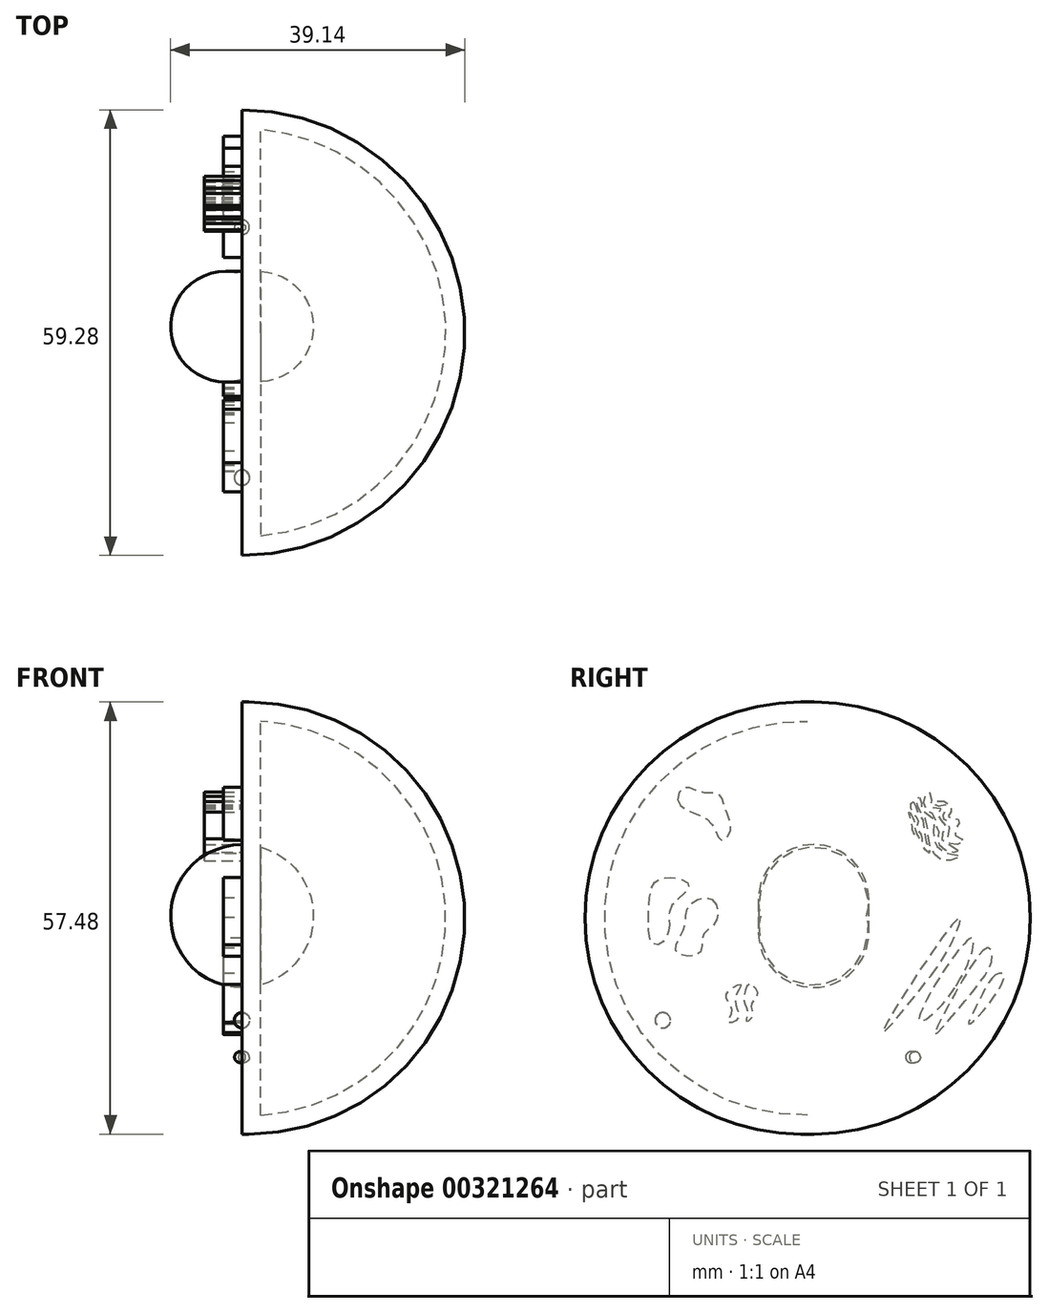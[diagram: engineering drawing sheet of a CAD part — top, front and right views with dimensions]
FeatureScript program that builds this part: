
annotation { "Feature Type Name" : "Feature", "Feature Type Description" : "" }
export const myFeature = defineFeature(function(context is Context, id is Id, definition is map)
    precondition{}
    {
        {
            var Q0;
            Q0=qCreatedBy(makeId("Front.planeOp"),FACE);
            var sketch = newSketch(context, id + "F0", { "sketchPlane" : qUnion([Q0])});
            skLineSegment(sketch, "E0", {"start": v(0, 0) * mm, "end": v(0, 57.46) * mm});
            skArc(sketch, "E1", {"start": v(0, 0) * mm, "mid": v(29.64, 28.73) * mm, "end": v(0, 57.46) * mm});
            skSolve(sketch);
        }
        {
            var Q0;
            Q0 = qSketchRegion(id + "F0", true);
            var Q1;
            Q1=sQuery(id+"F0.wireOp",EDGE,"E0");
            revolve(context, id + "F1", {"entities" : qUnion([Q0]), "axis" : qUnion([Q1]), "revolveType" : RevolveType.SYMMETRIC, "angle" : 180 * degree});
        }
        {
            var Q0;
            Q0=makeQuery(id+"F1.opRevolve","CAP_FACE",FACE,{"disambiguationData":[OSD([sQuery(id+"F0.wireOp",EDGE,"E0"),sQuery(id+"F0.wireOp",EDGE,"E1")])],"isStart":false});
            var Q1;
            Q1=makeQuery(id+"F1.opRevolve","SWEPT_BODY",BODY,{"disambiguationData":[OSD([sQuery(id+"F0.wireOp",EDGE,"E0"),sQuery(id+"F0.wireOp",EDGE,"E1")])]});
            shell(context, id + "F2", {"isHollow" : true, "entities" : qUnion([Q0]), "parts" : qUnion([Q1]), "thickness" : 2.5 * mm});
        }
        {
            var Q0;
            Q0=qCreatedBy(makeId("Right.planeOp"),FACE);
            var sketch = newSketch(context, id + "F3", { "sketchPlane" : qUnion([Q0])});
            skLineSegment(sketch, "E2", {"start": v(7.83, 29) * mm, "end": v(-6.24, 29) * mm});
            skArc(sketch, "E3", {"start": v(7.83, 29) * mm, "mid": v(0.8, 38.5) * mm, "end": v(-6.24, 29) * mm});
            skSolve(sketch);
        }
        {
            var Q0;
            Q0 = qSketchRegion(id + "F3", true);
            var Q1;
            Q1=sQuery(id+"F3.wireOp",EDGE,"E2");
            revolve(context, id + "F4", {"operationType" : NewBodyOperationType.ADD, "entities" : qUnion([Q0]), "axis" : qUnion([Q1]), "revolveType" : RevolveType.ONE_DIRECTION, "angle" : 360 * degree});
        }
        {
            var Q0;
            Q0=makeQuery(id+"F1.opRevolve","CAP_FACE",FACE,{"disambiguationData":[OSD([sQuery(id+"F0.wireOp",EDGE,"E0"),sQuery(id+"F0.wireOp",EDGE,"E1")])],"isStart":false});
            var sketch = newSketch(context, id + "F5", { "sketchPlane" : qUnion([Q0])});
            skLineSegment(sketch, "E4", {"start": v(-14.03, 9.55) * mm, "end": v(-14.03, 10.91) * mm});
            skArc(sketch, "E5", {"start": v(-14.03, 10.91) * mm, "mid": v(-15, 10.23) * mm, "end": v(-14.03, 9.55) * mm});
            skSolve(sketch);
        }
        {
            var Q0;
            Q0 = qSketchRegion(id + "F5", true);
            var Q1;
            Q1=sQuery(id+"F5.wireOp",EDGE,"E4");
            revolve(context, id + "F6", {"entities" : qUnion([Q0]), "axis" : qUnion([Q1]), "revolveType" : RevolveType.FULL});
        }
        {
            var Q0;
            Q0=makeQuery(id+"F1.opRevolve","CAP_FACE",FACE,{"disambiguationData":[OSD([sQuery(id+"F0.wireOp",EDGE,"E0"),sQuery(id+"F0.wireOp",EDGE,"E1")])],"isStart":false});
            var sketch = newSketch(context, id + "F7", { "sketchPlane" : qUnion([Q0])});
            skEllipse(sketch, "E6", {"center": v(-17.37, 40.2) * mm, "majorRadius": 5.81 * mm, "minorRadius": 3.58 * mm, "majorAxis": v(0.42, 0.9)});
            skSolve(sketch);
        }
        {
            var Q0;
            Q0 = qSketchRegion(id + "F7", true);
            var Q1;
            Q1=sQuery(id+"F7.wireOp",EDGE,"E6");
            extrude(context, id + "F8", {"entities" : qUnion([Q0]), "bodyType" : ToolBodyType.SURFACE, "operationType" : NewBodyOperationType.ADD, "surfaceEntities" : qUnion([Q1]), "depth" : 5 * mm});
        }
        {
            var Q0;
            Q0=makeQuery(id+"F1.opRevolve","CAP_FACE",FACE,{"disambiguationData":[OSD([sQuery(id+"F0.wireOp",EDGE,"E0"),sQuery(id+"F0.wireOp",EDGE,"E1")])],"isStart":false});
            var sketch = newSketch(context, id + "F9", { "sketchPlane" : qUnion([Q0])});
            skFitSpline(sketch, "E7", {"points": [v(-17.23, 44.31) * mm, v(-19.19, 43.32) * mm, v(-18.73, 42.1) * mm, v(-20.22, 41.78) * mm, v(-19.53, 39.95) * mm, v(-20.82, 38.97) * mm, v(-18.9, 38.67) * mm, v(-18.84, 41.42) * mm, v(-18, 42.05) * mm, v(-18.5, 43.71) * mm, v(-17.06, 43.6) * mm, v(-17.23, 44.31) * mm]});
            skSolve(sketch);
        }
        {
            var Q0;
            Q0 = qSketchRegion(id + "F9", true);
            extrude(context, id + "F10", {"entities" : qUnion([Q0]), "depth" : 5 * mm});
        }
        {
            var Q0;
            Q0=makeQuery(id+"F1.opRevolve","CAP_FACE",FACE,{"disambiguationData":[OSD([sQuery(id+"F0.wireOp",EDGE,"E0"),sQuery(id+"F0.wireOp",EDGE,"E1")])],"isStart":false});
            var sketch = newSketch(context, id + "F11", { "sketchPlane" : qUnion([Q0])});
            skFitSpline(sketch, "E8", {"points": [v(-20.04, 37.68) * mm, v(-17.83, 39.3) * mm, v(-18.45, 41) * mm, v(-17.3, 42.39) * mm, v(-17.76, 43.35) * mm, v(-16.54, 43.34) * mm, v(-16.56, 44.83) * mm, v(-15.88, 45.44) * mm, v(-15.54, 43.4) * mm, v(-16.67, 42.57) * mm, v(-17.18, 40.8) * mm, v(-17.46, 40.28) * mm, v(-17.37, 38.77) * mm, v(-19.06, 37.55) * mm, v(-20.04, 37.68) * mm]});
            skSolve(sketch);
        }
        {
            var Q0;
            Q0 = qSketchRegion(id + "F11", true);
            extrude(context, id + "F12", {"entities" : qUnion([Q0]), "operationType" : NewBodyOperationType.ADD, "depth" : 5 * mm});
        }
        {
            var Q0;
            Q0=makeQuery(id+"F1.opRevolve","CAP_FACE",FACE,{"disambiguationData":[OSD([sQuery(id+"F0.wireOp",EDGE,"E0"),sQuery(id+"F0.wireOp",EDGE,"E1")])],"isStart":false});
            var sketch = newSketch(context, id + "F13", { "sketchPlane" : qUnion([Q0])});
            skFitSpline(sketch, "E9", {"points": [v(-19.9, 36.75) * mm, v(-17.85, 36.46) * mm, v(-16.17, 38.81) * mm, v(-15.73, 41.79) * mm, v(-14.8, 43.18) * mm, v(-14.63, 44.9) * mm, v(-15.07, 44.5) * mm, v(-15.2, 43.16) * mm, v(-16.5, 42.2) * mm, v(-16.77, 40.51) * mm, v(-17.04, 38.58) * mm, v(-18.78, 37.27) * mm, v(-19.97, 37.1) * mm, v(-19.9, 36.75) * mm]});
            skSolve(sketch);
        }
        {
            var Q0;
            Q0 = qSketchRegion(id + "F13", true);
            extrude(context, id + "F14", {"entities" : qUnion([Q0]), "depth" : 5 * mm});
        }
        {
            var Q0;
            Q0=makeQuery(id+"F1.opRevolve","CAP_FACE",FACE,{"disambiguationData":[OSD([sQuery(id+"F0.wireOp",EDGE,"E0"),sQuery(id+"F0.wireOp",EDGE,"E1")])],"isStart":false});
            var sketch = newSketch(context, id + "F15", { "sketchPlane" : qUnion([Q0])});
            skFitSpline(sketch, "E10", {"points": [v(-14.1, 44.2) * mm, v(-14.78, 42.45) * mm, v(-15.3, 41.89) * mm, v(-15.46, 40.73) * mm, v(-15.75, 38.96) * mm, v(-15.94, 38.38) * mm, v(-16.24, 37.35) * mm, v(-15.31, 38.38) * mm, v(-15.24, 39.62) * mm, v(-14.63, 40.63) * mm, v(-14.75, 41.76) * mm, v(-14.14, 42.53) * mm, v(-13.72, 43.86) * mm, v(-14.1, 44.2) * mm]});
            skSolve(sketch);
        }
        {
            var Q0;
            Q0 = qSketchRegion(id + "F15", true);
            extrude(context, id + "F16", {"entities" : qUnion([Q0]), "depth" : 5 * mm});
        }
        {
            var Q0;
            Q0=makeQuery(id+"F1.opRevolve","CAP_FACE",FACE,{"disambiguationData":[OSD([sQuery(id+"F0.wireOp",EDGE,"E0"),sQuery(id+"F0.wireOp",EDGE,"E1")])],"isStart":false});
            var sketch = newSketch(context, id + "F17", { "sketchPlane" : qUnion([Q0])});
            skFitSpline(sketch, "E11", {"points": [v(-13.53, 42.82) * mm, v(-14.02, 42.12) * mm, v(-14.25, 41.02) * mm, v(-14.52, 39.92) * mm, v(-14.84, 39.3) * mm, v(-14.17, 39.94) * mm, v(-13.84, 41.38) * mm, v(-13.53, 42.82) * mm]});
            skSolve(sketch);
        }
        {
            var Q0;
            Q0 = qSketchRegion(id + "F17", true);
            extrude(context, id + "F18", {"entities" : qUnion([Q0]), "depth" : 5 * mm});
        }
        {
            var Q0;
            Q0=makeQuery(id+"F1.opRevolve","CAP_FACE",FACE,{"disambiguationData":[OSD([sQuery(id+"F0.wireOp",EDGE,"E0"),sQuery(id+"F0.wireOp",EDGE,"E1")])],"isStart":false});
            var sketch = newSketch(context, id + "F19", { "sketchPlane" : qUnion([Q0])});
            skFitSpline(sketch, "E12", {"points": [v(17.3, 44.5) * mm, v(15.8, 42.97) * mm, v(13.58, 42.04) * mm, v(12.18, 40.22) * mm, v(11.46, 39.1) * mm, v(10.2, 40.4) * mm, v(11.14, 43.73) * mm, v(11.82, 45.21) * mm, v(14.21, 45.46) * mm, v(16.38, 46.13) * mm, v(17.3, 44.5) * mm]});
            skSolve(sketch);
        }
        {
            var Q0;
            Q0 = qSketchRegion(id + "F19", true);
            extrude(context, id + "F20", {"entities" : qUnion([Q0]), "depth" : 2.5 * mm});
        }
        {
            var Q0;
            Q0=makeQuery(id+"F1.opRevolve","CAP_FACE",FACE,{"disambiguationData":[OSD([sQuery(id+"F0.wireOp",EDGE,"E0"),sQuery(id+"F0.wireOp",EDGE,"E1")])],"isStart":false});
            var sketch = newSketch(context, id + "F21", { "sketchPlane" : qUnion([Q0])});
            skFitSpline(sketch, "E13", {"points": [v(8.94, 19.88) * mm, v(9.63, 18) * mm, v(9.24, 15.4) * mm, v(10.58, 14.85) * mm, v(10.04, 16.45) * mm, v(10.86, 18.5) * mm, v(8.94, 19.88) * mm]});
            skSolve(sketch);
        }
        {
            var Q0;
            Q0 = qSketchRegion(id + "F21", true);
            extrude(context, id + "F22", {"entities" : qUnion([Q0]), "operationType" : NewBodyOperationType.ADD, "depth" : 2.5 * mm});
        }
        {
            var Q0;
            Q0=makeQuery(id+"F1.opRevolve","CAP_FACE",FACE,{"disambiguationData":[OSD([sQuery(id+"F0.wireOp",EDGE,"E0"),sQuery(id+"F0.wireOp",EDGE,"E1")])],"isStart":false});
            var sketch = newSketch(context, id + "F23", { "sketchPlane" : qUnion([Q0])});
            skFitSpline(sketch, "E14", {"points": [v(7.78, 19.88) * mm, v(8.36, 18.7) * mm, v(8.44, 17.54) * mm, v(8, 16.17) * mm, v(8.16, 15.03) * mm, v(7.3, 15.74) * mm, v(7.46, 17.2) * mm, v(6.6, 18.71) * mm, v(7.78, 19.88) * mm]});
            skSolve(sketch);
        }
        {
            var Q0;
            Q0 = qSketchRegion(id + "F23", true);
            extrude(context, id + "F24", {"entities" : qUnion([Q0]), "operationType" : NewBodyOperationType.ADD, "depth" : 2.5 * mm});
        }
        {
            var Q0;
            Q0=makeQuery(id+"F1.opRevolve","CAP_FACE",FACE,{"disambiguationData":[OSD([sQuery(id+"F0.wireOp",EDGE,"E0"),sQuery(id+"F0.wireOp",EDGE,"E1")])],"isStart":false});
            var sketch = newSketch(context, id + "F25", { "sketchPlane" : qUnion([Q0])});
            skFitSpline(sketch, "E15", {"points": [v(12.71, 31.22) * mm, v(12.22, 28.2) * mm, v(13.92, 26.4) * mm, v(14.44, 24) * mm, v(17.5, 24.28) * mm, v(16.46, 27.34) * mm, v(15.75, 30.38) * mm, v(12.71, 31.22) * mm]});
            skFitSpline(sketch, "E16", {"points": [v(18.4, 27.87) * mm, v(19.18, 25.66) * mm, v(20.57, 25.3) * mm, v(21.12, 30.38) * mm, v(19.6, 34) * mm, v(15.75, 33.1) * mm, v(18.06, 30.38) * mm, v(18.4, 27.87) * mm]});
            skSolve(sketch);
        }
        {
            var Q0;
            Q0=makeQuery(id+"F25.imprint","IMPRINT",FACE,{"disambiguationData":[TD([[makeQuery(id+"F25.imprint","IMPRINT",EDGE,{"derivedFrom":sQuery(id+"F25.wireOp",EDGE,"E16")}),1.0]])]});
            var Q1;
            Q1 = qSketchRegion(id + "F25", true);
            var Q2;
            Q2=makeQuery(id+"F25.imprint","IMPRINT",FACE,{"disambiguationData":[TD([[makeQuery(id+"F25.imprint","IMPRINT",EDGE,{"derivedFrom":sQuery(id+"F25.wireOp",EDGE,"E15")}),1.0]])]});
            extrude(context, id + "F26", {"entities" : qUnion([Q0, Q1, Q2]), "depth" : 2.5 * mm});
        }
        {
            var Q0;
            Q0=makeQuery(id+"F1.opRevolve","CAP_FACE",FACE,{"disambiguationData":[OSD([sQuery(id+"F0.wireOp",EDGE,"E0"),sQuery(id+"F0.wireOp",EDGE,"E1")])],"isStart":false});
            var sketch = newSketch(context, id + "F27", { "sketchPlane" : qUnion([Q0])});
            skFitSpline(sketch, "E17", {"points": [v(-21.68, 26.03) * mm, v(-14.87, 15.3) * mm, v(-19.84, 19.82) * mm, v(-21.68, 26.03) * mm]});
            skFitSpline(sketch, "E18", {"points": [v(-20.2, 28.83) * mm, v(-10, 13.63) * mm, v(-15.13, 19.46) * mm, v(-19.34, 25.79) * mm, v(-20.2, 28.83) * mm]});
            skFitSpline(sketch, "E19", {"points": [v(-24, 24.78) * mm, v(-18.27, 16.22) * mm, v(-16.99, 13.27) * mm, v(-21.44, 18.3) * mm, v(-24.54, 23.3) * mm, v(-24, 24.78) * mm]});
            skFitSpline(sketch, "E20", {"points": [v(-25, 21.16) * mm, v(-22.65, 17.38) * mm, v(-21.44, 14.63) * mm, v(-23.83, 16.95) * mm, v(-26.11, 21.2) * mm, v(-25, 21.16) * mm]});
            skFitSpline(sketch, "E21", {"points": [v(-16.4, 21.07) * mm, v(-19.84, 19.82) * mm, v(-17.82, 18.83) * mm, v(-16.9, 17.94) * mm], "startDerivative": vector(-12.68, -3.04) * mm, "endDerivative": vector(2.44, -3.7) * mm});
            skSolve(sketch);
        }
        {
            var Q0;
            {var subQ0=sQuery(id+"F27.wireOp",EDGE,"E21");var subQ1=sQuery(id+"F27.wireOp",EDGE,"E17");var subQ2=makeQuery(id+"F27.imprint","INTERSECT",VERTEX,{"disambiguationData":[OD(0.0)],"derivedFrom":[subQ1,subQ0]});Q0=makeQuery(id+"F27.imprint","IMPRINT",FACE,{"disambiguationData":[TD([[makeQuery(id+"F27.imprint","IMPRINT",EDGE,{"disambiguationData":[TD([[subQ2,1.0]])],"derivedFrom":subQ1}),-1.0]])]});}
            var Q1;
            Q1 = qSketchRegion(id + "F27", true);
            var Q2;
            Q2=makeQuery(id+"F27.imprint","IMPRINT",FACE,{"disambiguationData":[TD([[makeQuery(id+"F27.imprint","IMPRINT",EDGE,{"derivedFrom":sQuery(id+"F27.wireOp",EDGE,"E19")}),-1.0]])]});
            var Q3;
            Q3=makeQuery(id+"F27.imprint","IMPRINT",FACE,{"disambiguationData":[TD([[makeQuery(id+"F27.imprint","IMPRINT",EDGE,{"derivedFrom":sQuery(id+"F27.wireOp",EDGE,"E20")}),-1.0]])]});
            var Q4;
            Q4=makeQuery(id+"F27.imprint","IMPRINT",FACE,{"disambiguationData":[TD([[makeQuery(id+"F27.imprint","IMPRINT",EDGE,{"derivedFrom":sQuery(id+"F27.wireOp",EDGE,"E18")}),-1.0]])]});
            var Q5;
            {var subQ0=sQuery(id+"F27.wireOp",EDGE,"E21");var subQ1=sQuery(id+"F27.wireOp",EDGE,"E17");var subQ2=makeQuery(id+"F27.imprint","INTERSECT",VERTEX,{"disambiguationData":[OD(1.0)],"derivedFrom":[subQ1,subQ0]});Q5=makeQuery(id+"F27.imprint","IMPRINT",FACE,{"disambiguationData":[TD([[makeQuery(id+"F27.imprint","IMPRINT",EDGE,{"disambiguationData":[TD([[subQ2,1.0]])],"derivedFrom":subQ1}),-1.0]])]});}
            extrude(context, id + "F28", {"entities" : qUnion([Q0, Q1, Q2, Q3, Q4, Q5]), "depth" : 2.5 * mm});
        }
        {
            var Q0;
            Q0=makeQuery(id+"F1.opRevolve","CAP_FACE",FACE,{"disambiguationData":[OSD([sQuery(id+"F0.wireOp",EDGE,"E0"),sQuery(id+"F0.wireOp",EDGE,"E1")])],"isStart":false});
            var sketch = newSketch(context, id + "F29", { "sketchPlane" : qUnion([Q0])});
            skLineSegment(sketch, "E22", {"start": v(20, 15.85) * mm, "end": v(18.55, 14.4) * mm});
            skArc(sketch, "E23", {"start": v(18.55, 14.4) * mm, "mid": v(19.98, 14.41) * mm, "end": v(20, 15.85) * mm});
            skSolve(sketch);
        }
        {
            var Q0;
            Q0 = qSketchRegion(id + "F29", true);
            var Q1;
            Q1=sQuery(id+"F29.wireOp",EDGE,"E22");
            revolve(context, id + "F30", {"entities" : qUnion([Q0]), "axis" : qUnion([Q1]), "revolveType" : RevolveType.FULL});
        }
    });
